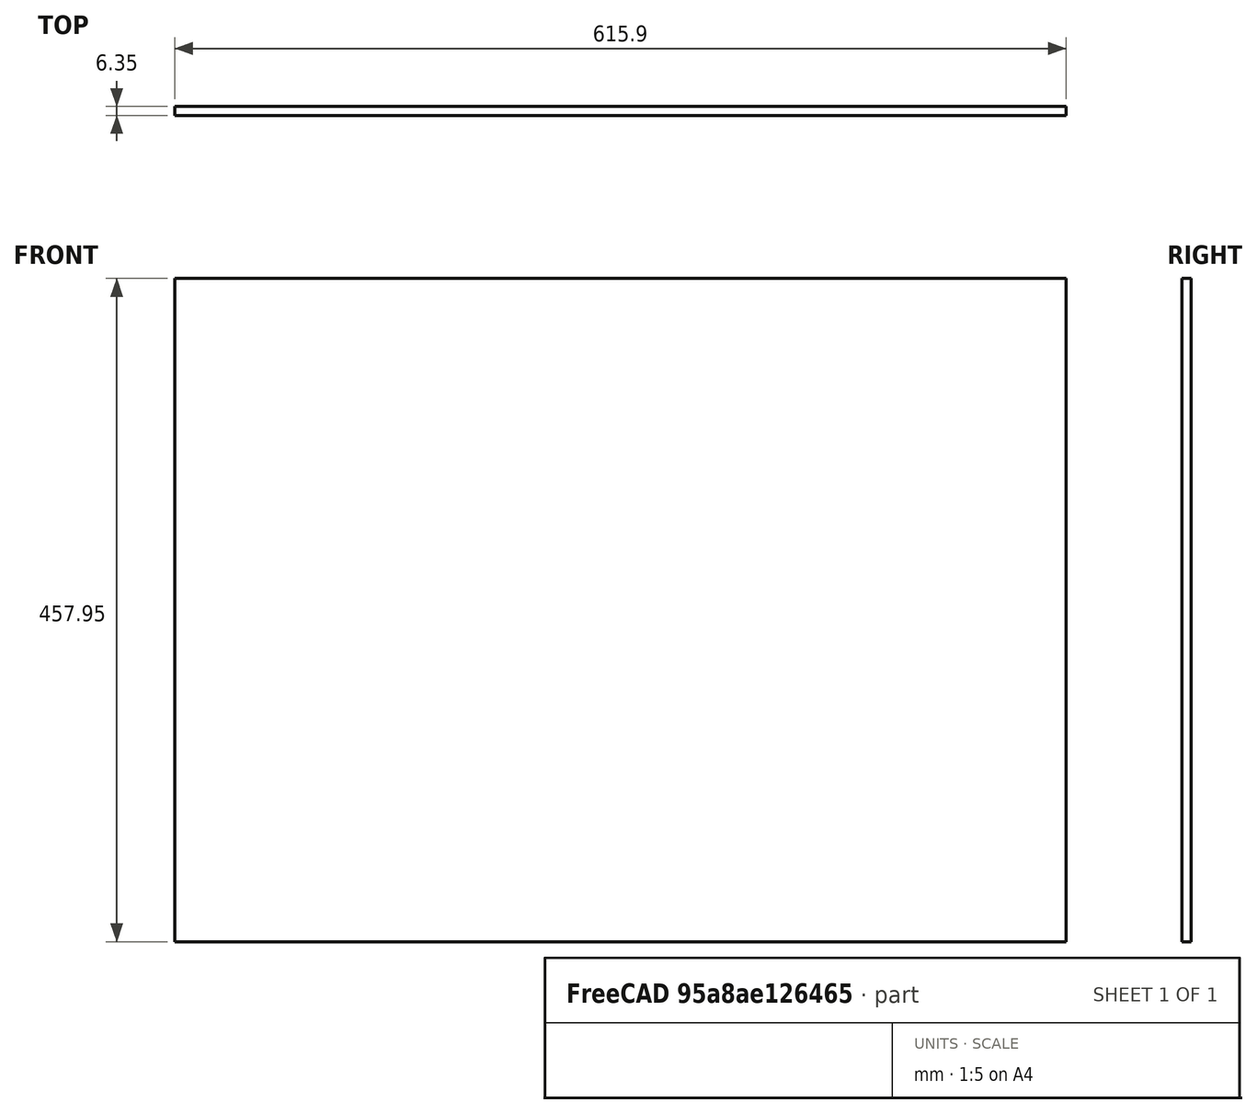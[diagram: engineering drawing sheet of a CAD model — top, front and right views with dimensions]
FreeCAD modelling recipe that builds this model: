
FCSTD DOCUMENT  (FreeCAD 0.19R24291 (Git))
Label: sidePanel
License: All rights reserved
LicenseURL: http://en.wikipedia.org/wiki/All_rights_reserved
objects: Sketcher::SketchObject×1, PartDesign::Pad×1, PartDesign::Body×1
note: 4 computed .brp shape members not serialized (recipe doc carries the construction recipe); baked Part::Feature solids carry a one-line shape summary decoded from their .brp

FEATURE [Sketcher::SketchObject] Sketch
  FullyConstrained = true
  MapMode = 5
  Placement = pos=(0,0,0) rot=(1,0,0;1.5708rad)
  Support = -> [XZ_Plane]
  expr: Constraints[10] = 605.2 + 2 * 1 / 4 * 25.4 - 1 - 1
  expr: Constraints[9] = 447.25 + 2 * 1 / 4 * 25.4 - 1 - 1
  sketch-geometry (4):
    g0: LineSegment StartX=0 StartY=0 StartZ=0 EndX=615.9 EndY=0 EndZ=0
    g1: LineSegment StartX=615.9 StartY=0 StartZ=0 EndX=615.9 EndY=457.95 EndZ=0
    g2: LineSegment StartX=615.9 StartY=457.95 StartZ=0 EndX=0 EndY=457.95 EndZ=0
    g3: LineSegment StartX=0 StartY=457.95 StartZ=0 EndX=0 EndY=0 EndZ=0
  constraints (11):
    c: Coincident(g0,g1)
    c: Coincident(g1,g2)
    c: Coincident(g2,g3)
    c: Coincident(g3,g0)
    c: Horizontal(g0)
    c: Horizontal(g2)
    c: Vertical(g1)
    c: Vertical(g3)
    c: Coincident(g0,g-1)
    c: DistanceY(g3,g3) = 457.95
    c: DistanceX(g0,g0) = 615.9
FEATURE [PartDesign::Pad] Pad
  Direction = (1,1,1)
  Length = 6.35
  Length2 = 100
  Placement = pos=(0,0,0) rot=(1,0,0;1.5708rad)
  Profile = -> Sketch
  Type = 0
  expr: Length = 1 / 4 * 25.4
FEATURE [PartDesign::Body] Body
  Group = -> [Sketch,Pad]
  Origin = -> Origin
  Tip = -> Pad
